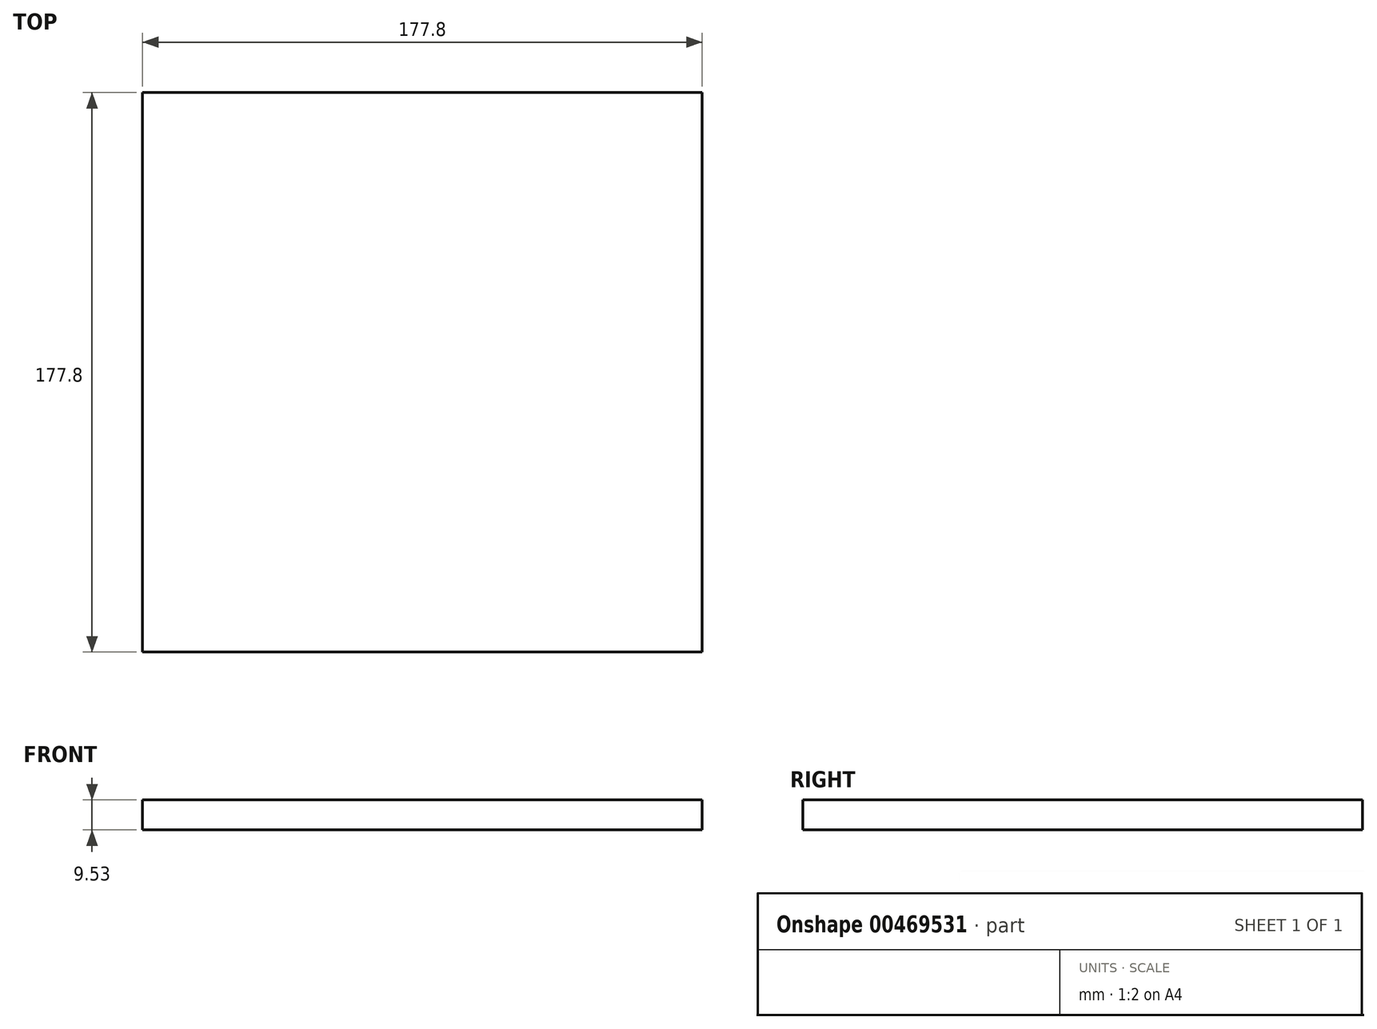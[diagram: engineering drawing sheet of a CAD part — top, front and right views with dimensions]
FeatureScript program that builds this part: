
annotation { "Feature Type Name" : "Feature", "Feature Type Description" : "" }
export const myFeature = defineFeature(function(context is Context, id is Id, definition is map)
    precondition{}
    {
        {
            var Q0;
            Q0=qCreatedBy(makeId("Top.planeOp"),FACE);
            var sketch = newSketch(context, id + "F0", { "sketchPlane" : qUnion([Q0])});
            skLineSegment(sketch, "E0.bottom", {"start": v(-88.9, -88.9) * mm, "end": v(88.9, -88.9) * mm});
            skLineSegment(sketch, "E0.top", {"start": v(-88.9, 88.9) * mm, "end": v(88.9, 88.9) * mm});
            skLineSegment(sketch, "E0.left", {"start": v(-88.9, -88.9) * mm, "end": v(-88.9, 88.9) * mm});
            skLineSegment(sketch, "E0.right", {"start": v(88.9, -88.9) * mm, "end": v(88.9, 88.9) * mm});
            skPoint(sketch, "E0.middle", {"position": v(0, 0) * mm});
            skSolve(sketch);
        }
        {
            var Q0;
            Q0 = qSketchRegion(id + "F0", true);
            extrude(context, id + "F1", {"entities" : qUnion([Q0]), "depth" : 9.52 * mm, "offsetDistance" : 25.4 * mm});
        }
    });
